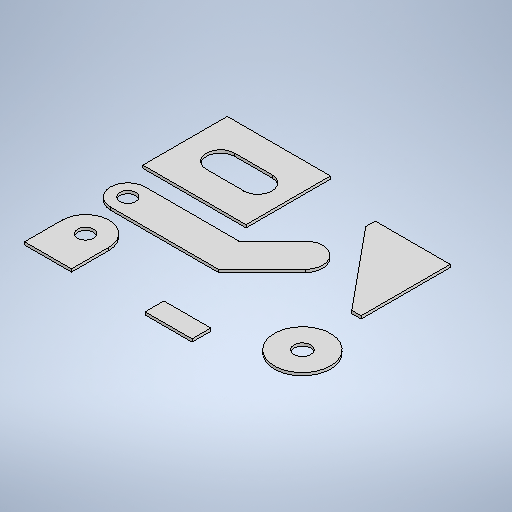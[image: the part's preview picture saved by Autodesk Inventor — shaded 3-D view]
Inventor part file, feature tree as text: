
AUTODESK INVENTOR PART (.ipt)
format: ipt  version: 2025.3 (Build 293356030, 356C)  size: 337,920 bytes
history: native  units: mm
features: other x2, sheet_metal_op x1, sketch x1
ambient origin geometry x8: Origin, YZ Plane, XZ Plane, XY Plane, X Axis, Y Axis, Z Axis, Center Point
bodies: Solid1 (feature_tree)
feature tree (4):
  sheet_metal_op  "Face1"
  sketch  "Sketch1"  dims[d2=3.0mm d22=50.0mm d23=20.0mm d24=17.0mm d25=10.0mm d26=100.0mm d28=135.0deg d29=50.0mm d30=17.0mm d31=25.0mm d32=40.0mm d33=80.0mm d34=95.0mm d35=10.0mm d36=10.0mm d37=110.0mm d38=30.0mm d39=40.0mm d40=60.0mm d41=18.0mm d42=6.0mm d43=90.0mm]
  other  "Plate1"
  other  "Definition1"
